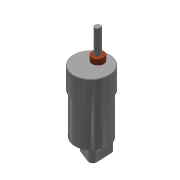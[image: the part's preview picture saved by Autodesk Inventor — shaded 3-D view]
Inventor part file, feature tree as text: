
AUTODESK INVENTOR PART (.ipt)
format: ipt  version: 2013 (Build 170138000, 138)  size: 215,040 bytes
history: native  units: in
note: dims shown in document units (in); Inventor stores cm internally (conversion verified against a paired STEP export)
features: other x4, sketch x4
ambient origin geometry x8: Origin, YZ Plane, XZ Plane, XY Plane, X Axis, Y Axis, Z Axis, Center Point
bodies: Solid1 (feature_tree), Solid2 (feature_tree)
feature tree (8):
  other  "Tetrix motor.ipt"
  other  "DC_MOTOR_2011::Tetrix motor.ipt"
  other  "Solid2::Tetrix motor.ipt"
  other  "TaggingFeature1"
  sketch  "Sketch1"  dims[d0=0.3937in]
  sketch  "Sketch2"  dims[d1=0.5909in d3=0.3436in d5=0.4528in d6=0.4528in d7=0.1654in d8=0.0in d9=0.748in d11=0.4331in d12=0.3661in d13=0.0in d14=0.2165in d16=0.0472in d17=0.0in d18=0.0197in d19=0.0787in d20=0.1181in d21=0.1181in d22=0.5906in d23=0.0in]
  sketch  "Sketch3"
  sketch  "Sketch4"
